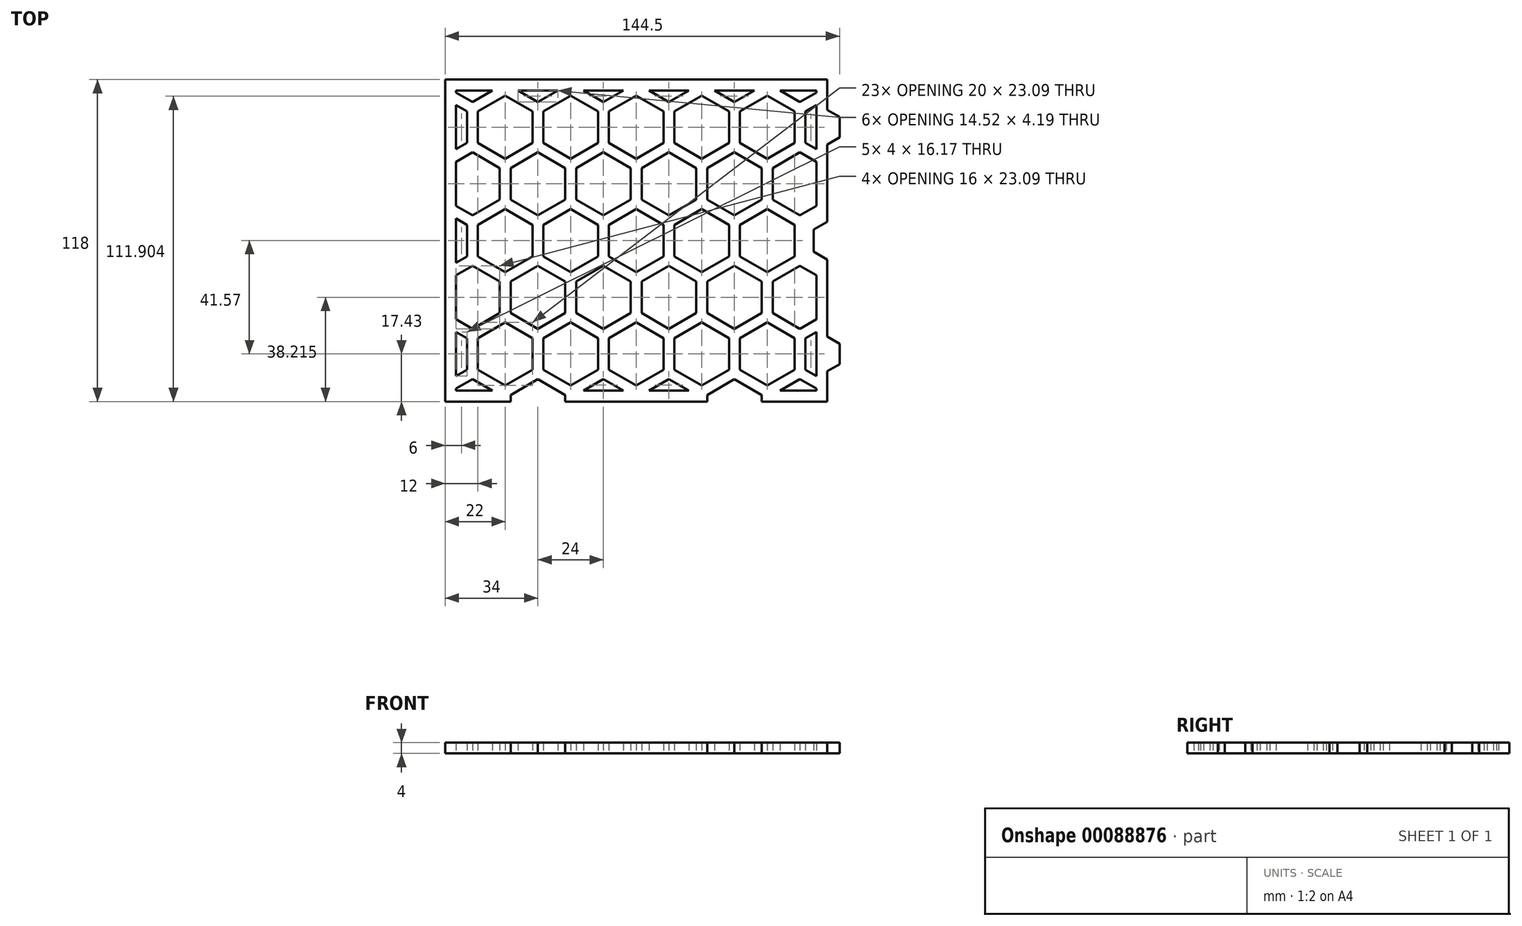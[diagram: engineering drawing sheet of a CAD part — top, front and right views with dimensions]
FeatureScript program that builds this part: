
annotation { "Feature Type Name" : "Feature", "Feature Type Description" : "" }
export const myFeature = defineFeature(function(context is Context, id is Id, definition is map)
    precondition{}
    {
        {
            var Q0;
            Q0=qCreatedBy(makeId("Top.planeOp"),FACE);
            var sketch = newSketch(context, id + "F0", { "sketchPlane" : qUnion([Q0])});
            skLineSegment(sketch, "E0.bottom", {"start": v(70, -59) * mm, "end": v(-70, -59) * mm});
            skLineSegment(sketch, "E0.top", {"start": v(70, 59) * mm, "end": v(-70, 59) * mm});
            skLineSegment(sketch, "E0.left", {"start": v(70, -59) * mm, "end": v(70, 59) * mm});
            skLineSegment(sketch, "E0.right", {"start": v(-70, -59) * mm, "end": v(-70, 59) * mm});
            skPoint(sketch, "E0.middle", {"position": v(0, 0) * mm});
            skLineSegment(sketch, "E1.0", {"start": v(-66, -55) * mm, "end": v(-66, 55) * mm});
            skLineSegment(sketch, "E1.1", {"start": v(66, -55) * mm, "end": v(-66, -55) * mm});
            skLineSegment(sketch, "E1.2", {"start": v(66, -55) * mm, "end": v(66, 55) * mm});
            skLineSegment(sketch, "E1.3", {"start": v(66, 55) * mm, "end": v(-66, 55) * mm});
            skSolve(sketch);
        }
        {
            var Q0;
            Q0=qSketchRegion(id+"F0",true);
            extrude(context, id + "F1", {"entities" : qUnion([Q0]), "depth" : 4 * mm});
        }
        {
            var Q0;
            Q0=qCreatedBy(makeId("Top.planeOp"),FACE);
            var sketch = newSketch(context, id + "F2", { "sketchPlane" : qUnion([Q0])});
            skLineSegment(sketch, "E2.0.1.1", {"start": v(-62, -47.34) * mm, "end": v(-66, -49.65) * mm});
            skLineSegment(sketch, "E2.0.1.5", {"start": v(-66, -33.49) * mm, "end": v(-62, -35.8) * mm});
            skLineSegment(sketch, "E2.0.1.13", {"start": v(-62, -35.8) * mm, "end": v(-62, -47.34) * mm});
            skLineSegment(sketch, "E2.0.2.1", {"start": v(-62, -5.77) * mm, "end": v(-66, -8.08) * mm});
            skLineSegment(sketch, "E2.0.2.5", {"start": v(-66, 8.08) * mm, "end": v(-62, 5.77) * mm});
            skLineSegment(sketch, "E2.0.2.13", {"start": v(-62, 5.77) * mm, "end": v(-62, -5.77) * mm});
            skLineSegment(sketch, "E2.0.3.1", {"start": v(-62, 35.8) * mm, "end": v(-66, 33.49) * mm});
            skLineSegment(sketch, "E2.0.3.5", {"start": v(-66, 49.65) * mm, "end": v(-62, 47.34) * mm});
            skLineSegment(sketch, "E2.0.3.13", {"start": v(-62, 47.34) * mm, "end": v(-62, 35.8) * mm});
            skLineSegment(sketch, "E2.1.0.7", {"start": v(-60, -50.8) * mm, "end": v(-52.74, -55) * mm});
            skLineSegment(sketch, "E2.1.0.8", {"start": v(-66, -54.27) * mm, "end": v(-60, -50.8) * mm});
            skCircle(sketch, "E2.1.1.0", {"center": v(-48, -41.57) * mm, "radius": 11.55 * mm, "construction": true});
            skLineSegment(sketch, "E2.1.1.1", {"start": v(-38, -47.34) * mm, "end": v(-48, -53.12) * mm});
            skLineSegment(sketch, "E2.1.1.2", {"start": v(-48, -53.12) * mm, "end": v(-58, -47.34) * mm});
            skLineSegment(sketch, "E2.1.1.3", {"start": v(-58, -47.34) * mm, "end": v(-58, -35.8) * mm});
            skLineSegment(sketch, "E2.1.1.4", {"start": v(-58, -35.8) * mm, "end": v(-48, -30.02) * mm});
            skLineSegment(sketch, "E2.1.1.5", {"start": v(-48, -30.02) * mm, "end": v(-38, -35.8) * mm});
            skLineSegment(sketch, "E2.1.1.6", {"start": v(-50, -15.01) * mm, "end": v(-50, -26.56) * mm});
            skLineSegment(sketch, "E2.1.1.7", {"start": v(-60, -9.24) * mm, "end": v(-50, -15.01) * mm});
            skLineSegment(sketch, "E2.1.1.8", {"start": v(-66, -12.7) * mm, "end": v(-60, -9.24) * mm});
            skLineSegment(sketch, "E2.1.1.10", {"start": v(-60, -32.33) * mm, "end": v(-66, -28.87) * mm});
            skLineSegment(sketch, "E2.1.1.11", {"start": v(-50, -26.56) * mm, "end": v(-60, -32.33) * mm});
            skLineSegment(sketch, "E2.1.1.13", {"start": v(-38, -35.8) * mm, "end": v(-38, -47.34) * mm});
            skCircle(sketch, "E2.1.2.0", {"center": v(-48, 0) * mm, "radius": 11.55 * mm, "construction": true});
            skLineSegment(sketch, "E2.1.2.1", {"start": v(-38, -5.77) * mm, "end": v(-48, -11.55) * mm});
            skLineSegment(sketch, "E2.1.2.2", {"start": v(-48, -11.55) * mm, "end": v(-58, -5.77) * mm});
            skLineSegment(sketch, "E2.1.2.3", {"start": v(-58, -5.77) * mm, "end": v(-58, 5.77) * mm});
            skLineSegment(sketch, "E2.1.2.4", {"start": v(-58, 5.77) * mm, "end": v(-48, 11.55) * mm});
            skLineSegment(sketch, "E2.1.2.5", {"start": v(-48, 11.55) * mm, "end": v(-38, 5.77) * mm});
            skLineSegment(sketch, "E2.1.2.6", {"start": v(-50, 26.56) * mm, "end": v(-50, 15.01) * mm});
            skLineSegment(sketch, "E2.1.2.7", {"start": v(-60, 32.33) * mm, "end": v(-50, 26.56) * mm});
            skLineSegment(sketch, "E2.1.2.8", {"start": v(-66, 28.87) * mm, "end": v(-60, 32.33) * mm});
            skLineSegment(sketch, "E2.1.2.10", {"start": v(-60, 9.24) * mm, "end": v(-66, 12.7) * mm});
            skLineSegment(sketch, "E2.1.2.11", {"start": v(-50, 15.01) * mm, "end": v(-60, 9.24) * mm});
            skLineSegment(sketch, "E2.1.2.13", {"start": v(-38, 5.77) * mm, "end": v(-38, -5.77) * mm});
            skCircle(sketch, "E2.1.3.0", {"center": v(-48, 41.57) * mm, "radius": 11.55 * mm, "construction": true});
            skLineSegment(sketch, "E2.1.3.1", {"start": v(-38, 35.8) * mm, "end": v(-48, 30.02) * mm});
            skLineSegment(sketch, "E2.1.3.2", {"start": v(-48, 30.02) * mm, "end": v(-58, 35.8) * mm});
            skLineSegment(sketch, "E2.1.3.3", {"start": v(-58, 35.8) * mm, "end": v(-58, 47.34) * mm});
            skLineSegment(sketch, "E2.1.3.4", {"start": v(-58, 47.34) * mm, "end": v(-48, 53.12) * mm});
            skLineSegment(sketch, "E2.1.3.5", {"start": v(-48, 53.12) * mm, "end": v(-38, 47.34) * mm});
            skLineSegment(sketch, "E2.1.3.10", {"start": v(-60, 50.8) * mm, "end": v(-66, 54.27) * mm});
            skLineSegment(sketch, "E2.1.3.11", {"start": v(-52.74, 55) * mm, "end": v(-60, 50.8) * mm});
            skLineSegment(sketch, "E2.1.3.13", {"start": v(-38, 47.34) * mm, "end": v(-38, 35.8) * mm});
            skLineSegment(sketch, "E2.2.0.7", {"start": v(-36, -50.8) * mm, "end": v(-28.74, -55) * mm});
            skLineSegment(sketch, "E2.2.0.8", {"start": v(-43.26, -55) * mm, "end": v(-36, -50.8) * mm});
            skCircle(sketch, "E2.2.1.0", {"center": v(-24, -41.57) * mm, "radius": 11.55 * mm, "construction": true});
            skLineSegment(sketch, "E2.2.1.1", {"start": v(-14, -47.34) * mm, "end": v(-24, -53.12) * mm});
            skLineSegment(sketch, "E2.2.1.2", {"start": v(-24, -53.12) * mm, "end": v(-34, -47.34) * mm});
            skLineSegment(sketch, "E2.2.1.3", {"start": v(-34, -47.34) * mm, "end": v(-34, -35.8) * mm});
            skLineSegment(sketch, "E2.2.1.4", {"start": v(-34, -35.8) * mm, "end": v(-24, -30.02) * mm});
            skLineSegment(sketch, "E2.2.1.5", {"start": v(-24, -30.02) * mm, "end": v(-14, -35.8) * mm});
            skLineSegment(sketch, "E2.2.1.6", {"start": v(-26, -15.01) * mm, "end": v(-26, -26.56) * mm});
            skLineSegment(sketch, "E2.2.1.7", {"start": v(-36, -9.24) * mm, "end": v(-26, -15.01) * mm});
            skLineSegment(sketch, "E2.2.1.8", {"start": v(-46, -15.01) * mm, "end": v(-36, -9.24) * mm});
            skLineSegment(sketch, "E2.2.1.9", {"start": v(-46, -26.56) * mm, "end": v(-46, -15.01) * mm});
            skLineSegment(sketch, "E2.2.1.10", {"start": v(-36, -32.33) * mm, "end": v(-46, -26.56) * mm});
            skLineSegment(sketch, "E2.2.1.11", {"start": v(-26, -26.56) * mm, "end": v(-36, -32.33) * mm});
            skCircle(sketch, "E2.2.1.12", {"center": v(-36, -20.79) * mm, "radius": 11.55 * mm, "construction": true});
            skLineSegment(sketch, "E2.2.1.13", {"start": v(-14, -35.8) * mm, "end": v(-14, -47.34) * mm});
            skCircle(sketch, "E2.2.2.0", {"center": v(-24, 0) * mm, "radius": 11.55 * mm, "construction": true});
            skLineSegment(sketch, "E2.2.2.1", {"start": v(-14, -5.77) * mm, "end": v(-24, -11.55) * mm});
            skLineSegment(sketch, "E2.2.2.2", {"start": v(-24, -11.55) * mm, "end": v(-34, -5.77) * mm});
            skLineSegment(sketch, "E2.2.2.3", {"start": v(-34, -5.77) * mm, "end": v(-34, 5.77) * mm});
            skLineSegment(sketch, "E2.2.2.4", {"start": v(-34, 5.77) * mm, "end": v(-24, 11.55) * mm});
            skLineSegment(sketch, "E2.2.2.5", {"start": v(-24, 11.55) * mm, "end": v(-14, 5.77) * mm});
            skLineSegment(sketch, "E2.2.2.6", {"start": v(-26, 26.56) * mm, "end": v(-26, 15.01) * mm});
            skLineSegment(sketch, "E2.2.2.7", {"start": v(-36, 32.33) * mm, "end": v(-26, 26.56) * mm});
            skLineSegment(sketch, "E2.2.2.8", {"start": v(-46, 26.56) * mm, "end": v(-36, 32.33) * mm});
            skLineSegment(sketch, "E2.2.2.9", {"start": v(-46, 15.01) * mm, "end": v(-46, 26.56) * mm});
            skLineSegment(sketch, "E2.2.2.10", {"start": v(-36, 9.24) * mm, "end": v(-46, 15.01) * mm});
            skLineSegment(sketch, "E2.2.2.11", {"start": v(-26, 15.01) * mm, "end": v(-36, 9.24) * mm});
            skCircle(sketch, "E2.2.2.12", {"center": v(-36, 20.78) * mm, "radius": 11.55 * mm, "construction": true});
            skLineSegment(sketch, "E2.2.2.13", {"start": v(-14, 5.77) * mm, "end": v(-14, -5.77) * mm});
            skCircle(sketch, "E2.2.3.0", {"center": v(-24, 41.57) * mm, "radius": 11.55 * mm, "construction": true});
            skLineSegment(sketch, "E2.2.3.1", {"start": v(-14, 35.8) * mm, "end": v(-24, 30.02) * mm});
            skLineSegment(sketch, "E2.2.3.2", {"start": v(-24, 30.02) * mm, "end": v(-34, 35.8) * mm});
            skLineSegment(sketch, "E2.2.3.3", {"start": v(-34, 35.8) * mm, "end": v(-34, 47.34) * mm});
            skLineSegment(sketch, "E2.2.3.4", {"start": v(-34, 47.34) * mm, "end": v(-24, 53.12) * mm});
            skLineSegment(sketch, "E2.2.3.5", {"start": v(-24, 53.12) * mm, "end": v(-14, 47.34) * mm});
            skLineSegment(sketch, "E2.2.3.10", {"start": v(-36, 50.8) * mm, "end": v(-43.26, 55) * mm});
            skLineSegment(sketch, "E2.2.3.11", {"start": v(-28.74, 55) * mm, "end": v(-36, 50.8) * mm});
            skLineSegment(sketch, "E2.2.3.13", {"start": v(-14, 47.34) * mm, "end": v(-14, 35.8) * mm});
            skLineSegment(sketch, "E2.3.0.7", {"start": v(-12, -50.8) * mm, "end": v(-4.74, -55) * mm});
            skLineSegment(sketch, "E2.3.0.8", {"start": v(-19.26, -55) * mm, "end": v(-12, -50.8) * mm});
            skCircle(sketch, "E2.3.1.0", {"center": v(0, -41.57) * mm, "radius": 11.55 * mm, "construction": true});
            skLineSegment(sketch, "E2.3.1.1", {"start": v(10, -47.34) * mm, "end": v(0, -53.12) * mm});
            skLineSegment(sketch, "E2.3.1.2", {"start": v(0, -53.12) * mm, "end": v(-10, -47.34) * mm});
            skLineSegment(sketch, "E2.3.1.3", {"start": v(-10, -47.34) * mm, "end": v(-10, -35.8) * mm});
            skLineSegment(sketch, "E2.3.1.4", {"start": v(-10, -35.8) * mm, "end": v(0, -30.02) * mm});
            skLineSegment(sketch, "E2.3.1.5", {"start": v(0, -30.02) * mm, "end": v(10, -35.8) * mm});
            skLineSegment(sketch, "E2.3.1.6", {"start": v(-2, -15.01) * mm, "end": v(-2, -26.56) * mm});
            skLineSegment(sketch, "E2.3.1.7", {"start": v(-12, -9.24) * mm, "end": v(-2, -15.01) * mm});
            skLineSegment(sketch, "E2.3.1.8", {"start": v(-22, -15.01) * mm, "end": v(-12, -9.24) * mm});
            skLineSegment(sketch, "E2.3.1.9", {"start": v(-22, -26.56) * mm, "end": v(-22, -15.01) * mm});
            skLineSegment(sketch, "E2.3.1.10", {"start": v(-12, -32.33) * mm, "end": v(-22, -26.56) * mm});
            skLineSegment(sketch, "E2.3.1.11", {"start": v(-2, -26.56) * mm, "end": v(-12, -32.33) * mm});
            skCircle(sketch, "E2.3.1.12", {"center": v(-12, -20.79) * mm, "radius": 11.55 * mm, "construction": true});
            skLineSegment(sketch, "E2.3.1.13", {"start": v(10, -35.8) * mm, "end": v(10, -47.34) * mm});
            skCircle(sketch, "E2.3.2.0", {"center": v(0, 0) * mm, "radius": 11.55 * mm, "construction": true});
            skLineSegment(sketch, "E2.3.2.1", {"start": v(10, -5.77) * mm, "end": v(0, -11.55) * mm});
            skLineSegment(sketch, "E2.3.2.2", {"start": v(0, -11.55) * mm, "end": v(-10, -5.77) * mm});
            skLineSegment(sketch, "E2.3.2.3", {"start": v(-10, -5.77) * mm, "end": v(-10, 5.77) * mm});
            skLineSegment(sketch, "E2.3.2.4", {"start": v(-10, 5.77) * mm, "end": v(0, 11.55) * mm});
            skLineSegment(sketch, "E2.3.2.5", {"start": v(0, 11.55) * mm, "end": v(10, 5.77) * mm});
            skLineSegment(sketch, "E2.3.2.6", {"start": v(-2, 26.56) * mm, "end": v(-2, 15.01) * mm});
            skLineSegment(sketch, "E2.3.2.7", {"start": v(-12, 32.33) * mm, "end": v(-2, 26.56) * mm});
            skLineSegment(sketch, "E2.3.2.8", {"start": v(-22, 26.56) * mm, "end": v(-12, 32.33) * mm});
            skLineSegment(sketch, "E2.3.2.9", {"start": v(-22, 15.01) * mm, "end": v(-22, 26.56) * mm});
            skLineSegment(sketch, "E2.3.2.10", {"start": v(-12, 9.24) * mm, "end": v(-22, 15.01) * mm});
            skLineSegment(sketch, "E2.3.2.11", {"start": v(-2, 15.01) * mm, "end": v(-12, 9.24) * mm});
            skCircle(sketch, "E2.3.2.12", {"center": v(-12, 20.78) * mm, "radius": 11.55 * mm, "construction": true});
            skLineSegment(sketch, "E2.3.2.13", {"start": v(10, 5.77) * mm, "end": v(10, -5.77) * mm});
            skCircle(sketch, "E2.3.3.0", {"center": v(0, 41.57) * mm, "radius": 11.55 * mm, "construction": true});
            skLineSegment(sketch, "E2.3.3.1", {"start": v(10, 35.8) * mm, "end": v(0, 30.02) * mm});
            skLineSegment(sketch, "E2.3.3.2", {"start": v(0, 30.02) * mm, "end": v(-10, 35.8) * mm});
            skLineSegment(sketch, "E2.3.3.3", {"start": v(-10, 35.8) * mm, "end": v(-10, 47.34) * mm});
            skLineSegment(sketch, "E2.3.3.4", {"start": v(-10, 47.34) * mm, "end": v(0, 53.12) * mm});
            skLineSegment(sketch, "E2.3.3.5", {"start": v(0, 53.12) * mm, "end": v(10, 47.34) * mm});
            skLineSegment(sketch, "E2.3.3.10", {"start": v(-12, 50.8) * mm, "end": v(-19.26, 55) * mm});
            skLineSegment(sketch, "E2.3.3.11", {"start": v(-4.74, 55) * mm, "end": v(-12, 50.8) * mm});
            skLineSegment(sketch, "E2.3.3.13", {"start": v(10, 47.34) * mm, "end": v(10, 35.8) * mm});
            skLineSegment(sketch, "E2.4.0.7", {"start": v(12, -50.8) * mm, "end": v(19.26, -55) * mm});
            skLineSegment(sketch, "E2.4.0.8", {"start": v(4.74, -55) * mm, "end": v(12, -50.8) * mm});
            skCircle(sketch, "E2.4.1.0", {"center": v(24, -41.57) * mm, "radius": 11.55 * mm, "construction": true});
            skLineSegment(sketch, "E2.4.1.1", {"start": v(34, -47.34) * mm, "end": v(24, -53.12) * mm});
            skLineSegment(sketch, "E2.4.1.2", {"start": v(24, -53.12) * mm, "end": v(14, -47.34) * mm});
            skLineSegment(sketch, "E2.4.1.3", {"start": v(14, -47.34) * mm, "end": v(14, -35.8) * mm});
            skLineSegment(sketch, "E2.4.1.4", {"start": v(14, -35.8) * mm, "end": v(24, -30.02) * mm});
            skLineSegment(sketch, "E2.4.1.5", {"start": v(24, -30.02) * mm, "end": v(34, -35.8) * mm});
            skLineSegment(sketch, "E2.4.1.6", {"start": v(22, -15.01) * mm, "end": v(22, -26.56) * mm});
            skLineSegment(sketch, "E2.4.1.7", {"start": v(12, -9.24) * mm, "end": v(22, -15.01) * mm});
            skLineSegment(sketch, "E2.4.1.8", {"start": v(2, -15.01) * mm, "end": v(12, -9.24) * mm});
            skLineSegment(sketch, "E2.4.1.9", {"start": v(2, -26.56) * mm, "end": v(2, -15.01) * mm});
            skLineSegment(sketch, "E2.4.1.10", {"start": v(12, -32.33) * mm, "end": v(2, -26.56) * mm});
            skLineSegment(sketch, "E2.4.1.11", {"start": v(22, -26.56) * mm, "end": v(12, -32.33) * mm});
            skCircle(sketch, "E2.4.1.12", {"center": v(12, -20.79) * mm, "radius": 11.55 * mm, "construction": true});
            skLineSegment(sketch, "E2.4.1.13", {"start": v(34, -35.8) * mm, "end": v(34, -47.34) * mm});
            skCircle(sketch, "E2.4.2.0", {"center": v(24, 0) * mm, "radius": 11.55 * mm, "construction": true});
            skLineSegment(sketch, "E2.4.2.1", {"start": v(34, -5.77) * mm, "end": v(24, -11.55) * mm});
            skLineSegment(sketch, "E2.4.2.2", {"start": v(24, -11.55) * mm, "end": v(14, -5.77) * mm});
            skLineSegment(sketch, "E2.4.2.3", {"start": v(14, -5.77) * mm, "end": v(14, 5.77) * mm});
            skLineSegment(sketch, "E2.4.2.4", {"start": v(14, 5.77) * mm, "end": v(24, 11.55) * mm});
            skLineSegment(sketch, "E2.4.2.5", {"start": v(24, 11.55) * mm, "end": v(34, 5.77) * mm});
            skLineSegment(sketch, "E2.4.2.6", {"start": v(22, 26.56) * mm, "end": v(22, 15.01) * mm});
            skLineSegment(sketch, "E2.4.2.7", {"start": v(12, 32.33) * mm, "end": v(22, 26.56) * mm});
            skLineSegment(sketch, "E2.4.2.8", {"start": v(2, 26.56) * mm, "end": v(12, 32.33) * mm});
            skLineSegment(sketch, "E2.4.2.9", {"start": v(2, 15.01) * mm, "end": v(2, 26.56) * mm});
            skLineSegment(sketch, "E2.4.2.10", {"start": v(12, 9.24) * mm, "end": v(2, 15.01) * mm});
            skLineSegment(sketch, "E2.4.2.11", {"start": v(22, 15.01) * mm, "end": v(12, 9.24) * mm});
            skCircle(sketch, "E2.4.2.12", {"center": v(12, 20.78) * mm, "radius": 11.55 * mm, "construction": true});
            skLineSegment(sketch, "E2.4.2.13", {"start": v(34, 5.77) * mm, "end": v(34, -5.77) * mm});
            skCircle(sketch, "E2.4.3.0", {"center": v(24, 41.57) * mm, "radius": 11.55 * mm, "construction": true});
            skLineSegment(sketch, "E2.4.3.1", {"start": v(34, 35.8) * mm, "end": v(24, 30.02) * mm});
            skLineSegment(sketch, "E2.4.3.2", {"start": v(24, 30.02) * mm, "end": v(14, 35.8) * mm});
            skLineSegment(sketch, "E2.4.3.3", {"start": v(14, 35.8) * mm, "end": v(14, 47.34) * mm});
            skLineSegment(sketch, "E2.4.3.4", {"start": v(14, 47.34) * mm, "end": v(24, 53.12) * mm});
            skLineSegment(sketch, "E2.4.3.5", {"start": v(24, 53.12) * mm, "end": v(34, 47.34) * mm});
            skLineSegment(sketch, "E2.4.3.10", {"start": v(12, 50.8) * mm, "end": v(4.74, 55) * mm});
            skLineSegment(sketch, "E2.4.3.11", {"start": v(19.26, 55) * mm, "end": v(12, 50.8) * mm});
            skLineSegment(sketch, "E2.4.3.13", {"start": v(34, 47.34) * mm, "end": v(34, 35.8) * mm});
            skLineSegment(sketch, "E2.5.0.7", {"start": v(36, -50.8) * mm, "end": v(43.26, -55) * mm});
            skLineSegment(sketch, "E2.5.0.8", {"start": v(28.74, -55) * mm, "end": v(36, -50.8) * mm});
            skCircle(sketch, "E2.5.1.0", {"center": v(48, -41.57) * mm, "radius": 11.55 * mm, "construction": true});
            skLineSegment(sketch, "E2.5.1.1", {"start": v(58, -47.34) * mm, "end": v(48, -53.12) * mm});
            skLineSegment(sketch, "E2.5.1.2", {"start": v(48, -53.12) * mm, "end": v(38, -47.34) * mm});
            skLineSegment(sketch, "E2.5.1.3", {"start": v(38, -47.34) * mm, "end": v(38, -35.8) * mm});
            skLineSegment(sketch, "E2.5.1.4", {"start": v(38, -35.8) * mm, "end": v(48, -30.02) * mm});
            skLineSegment(sketch, "E2.5.1.5", {"start": v(48, -30.02) * mm, "end": v(58, -35.8) * mm});
            skLineSegment(sketch, "E2.5.1.6", {"start": v(46, -15.01) * mm, "end": v(46, -26.56) * mm});
            skLineSegment(sketch, "E2.5.1.7", {"start": v(36, -9.24) * mm, "end": v(46, -15.01) * mm});
            skLineSegment(sketch, "E2.5.1.8", {"start": v(26, -15.01) * mm, "end": v(36, -9.24) * mm});
            skLineSegment(sketch, "E2.5.1.9", {"start": v(26, -26.56) * mm, "end": v(26, -15.01) * mm});
            skLineSegment(sketch, "E2.5.1.10", {"start": v(36, -32.33) * mm, "end": v(26, -26.56) * mm});
            skLineSegment(sketch, "E2.5.1.11", {"start": v(46, -26.56) * mm, "end": v(36, -32.33) * mm});
            skCircle(sketch, "E2.5.1.12", {"center": v(36, -20.79) * mm, "radius": 11.55 * mm, "construction": true});
            skLineSegment(sketch, "E2.5.1.13", {"start": v(58, -35.8) * mm, "end": v(58, -47.34) * mm});
            skCircle(sketch, "E2.5.2.0", {"center": v(48, 0) * mm, "radius": 11.55 * mm, "construction": true});
            skLineSegment(sketch, "E2.5.2.1", {"start": v(58, -5.77) * mm, "end": v(48, -11.55) * mm});
            skLineSegment(sketch, "E2.5.2.2", {"start": v(48, -11.55) * mm, "end": v(38, -5.77) * mm});
            skLineSegment(sketch, "E2.5.2.3", {"start": v(38, -5.77) * mm, "end": v(38, 5.77) * mm});
            skLineSegment(sketch, "E2.5.2.4", {"start": v(38, 5.77) * mm, "end": v(48, 11.55) * mm});
            skLineSegment(sketch, "E2.5.2.5", {"start": v(48, 11.55) * mm, "end": v(58, 5.77) * mm});
            skLineSegment(sketch, "E2.5.2.6", {"start": v(46, 26.56) * mm, "end": v(46, 15.01) * mm});
            skLineSegment(sketch, "E2.5.2.7", {"start": v(36, 32.33) * mm, "end": v(46, 26.56) * mm});
            skLineSegment(sketch, "E2.5.2.8", {"start": v(26, 26.56) * mm, "end": v(36, 32.33) * mm});
            skLineSegment(sketch, "E2.5.2.9", {"start": v(26, 15.01) * mm, "end": v(26, 26.56) * mm});
            skLineSegment(sketch, "E2.5.2.10", {"start": v(36, 9.24) * mm, "end": v(26, 15.01) * mm});
            skLineSegment(sketch, "E2.5.2.11", {"start": v(46, 15.01) * mm, "end": v(36, 9.24) * mm});
            skCircle(sketch, "E2.5.2.12", {"center": v(36, 20.78) * mm, "radius": 11.55 * mm, "construction": true});
            skLineSegment(sketch, "E2.5.2.13", {"start": v(58, 5.77) * mm, "end": v(58, -5.77) * mm});
            skCircle(sketch, "E2.5.3.0", {"center": v(48, 41.57) * mm, "radius": 11.55 * mm, "construction": true});
            skLineSegment(sketch, "E2.5.3.1", {"start": v(58, 35.8) * mm, "end": v(48, 30.02) * mm});
            skLineSegment(sketch, "E2.5.3.2", {"start": v(48, 30.02) * mm, "end": v(38, 35.8) * mm});
            skLineSegment(sketch, "E2.5.3.3", {"start": v(38, 35.8) * mm, "end": v(38, 47.34) * mm});
            skLineSegment(sketch, "E2.5.3.4", {"start": v(38, 47.34) * mm, "end": v(48, 53.12) * mm});
            skLineSegment(sketch, "E2.5.3.5", {"start": v(48, 53.12) * mm, "end": v(58, 47.34) * mm});
            skLineSegment(sketch, "E2.5.3.10", {"start": v(36, 50.8) * mm, "end": v(28.74, 55) * mm});
            skLineSegment(sketch, "E2.5.3.11", {"start": v(43.26, 55) * mm, "end": v(36, 50.8) * mm});
            skLineSegment(sketch, "E2.5.3.13", {"start": v(58, 47.34) * mm, "end": v(58, 35.8) * mm});
            skLineSegment(sketch, "E2.6.0.7", {"start": v(60, -50.8) * mm, "end": v(66, -54.27) * mm});
            skLineSegment(sketch, "E2.6.0.8", {"start": v(52.74, -55) * mm, "end": v(60, -50.8) * mm});
            skLineSegment(sketch, "E2.6.1.2", {"start": v(66, -49.65) * mm, "end": v(62, -47.34) * mm});
            skLineSegment(sketch, "E2.6.1.3", {"start": v(62, -47.34) * mm, "end": v(62, -35.8) * mm});
            skLineSegment(sketch, "E2.6.1.4", {"start": v(62, -35.8) * mm, "end": v(66, -33.49) * mm});
            skLineSegment(sketch, "E2.6.1.7", {"start": v(60, -9.24) * mm, "end": v(66, -12.7) * mm});
            skLineSegment(sketch, "E2.6.1.8", {"start": v(50, -15.01) * mm, "end": v(60, -9.24) * mm});
            skLineSegment(sketch, "E2.6.1.9", {"start": v(50, -26.56) * mm, "end": v(50, -15.01) * mm});
            skLineSegment(sketch, "E2.6.1.10", {"start": v(60, -32.33) * mm, "end": v(50, -26.56) * mm});
            skLineSegment(sketch, "E2.6.1.11", {"start": v(66, -28.87) * mm, "end": v(60, -32.33) * mm});
            skLineSegment(sketch, "E2.6.2.2", {"start": v(66, -8.08) * mm, "end": v(62, -5.77) * mm});
            skLineSegment(sketch, "E2.6.2.3", {"start": v(62, -5.77) * mm, "end": v(62, 5.77) * mm});
            skLineSegment(sketch, "E2.6.2.4", {"start": v(62, 5.77) * mm, "end": v(66, 8.08) * mm});
            skLineSegment(sketch, "E2.6.2.7", {"start": v(60, 32.33) * mm, "end": v(66, 28.87) * mm});
            skLineSegment(sketch, "E2.6.2.8", {"start": v(50, 26.56) * mm, "end": v(60, 32.33) * mm});
            skLineSegment(sketch, "E2.6.2.9", {"start": v(50, 15.01) * mm, "end": v(50, 26.56) * mm});
            skLineSegment(sketch, "E2.6.2.10", {"start": v(60, 9.24) * mm, "end": v(50, 15.01) * mm});
            skLineSegment(sketch, "E2.6.2.11", {"start": v(66, 12.7) * mm, "end": v(60, 9.24) * mm});
            skLineSegment(sketch, "E2.6.3.2", {"start": v(66, 33.49) * mm, "end": v(62, 35.8) * mm});
            skLineSegment(sketch, "E2.6.3.3", {"start": v(62, 35.8) * mm, "end": v(62, 47.34) * mm});
            skLineSegment(sketch, "E2.6.3.4", {"start": v(62, 47.34) * mm, "end": v(66, 49.65) * mm});
            skLineSegment(sketch, "E2.6.3.10", {"start": v(60, 50.8) * mm, "end": v(52.74, 55) * mm});
            skLineSegment(sketch, "E2.6.3.11", {"start": v(66, 54.27) * mm, "end": v(60, 50.8) * mm});
            skLineSegment(sketch, "E3.0", {"start": v(-66, -55) * mm, "end": v(-66, -54.27) * mm});
            skLineSegment(sketch, "E3.1", {"start": v(66, 55) * mm, "end": v(52.74, 55) * mm});
            skLineSegment(sketch, "E3.2", {"start": v(66, -55) * mm, "end": v(66, -54.27) * mm});
            skLineSegment(sketch, "E3.3", {"start": v(66, -55) * mm, "end": v(52.74, -55) * mm});
            skLineSegment(sketch, "E4.trimOffspring", {"start": v(-66, 54.27) * mm, "end": v(-66, 55) * mm});
            skLineSegment(sketch, "E5.trimOffspring", {"start": v(-66, 33.49) * mm, "end": v(-66, 49.65) * mm});
            skLineSegment(sketch, "E6.trimOffspring", {"start": v(-66, 12.7) * mm, "end": v(-66, 28.87) * mm});
            skLineSegment(sketch, "E7.trimOffspring", {"start": v(-52.74, 55) * mm, "end": v(-66, 55) * mm});
            skLineSegment(sketch, "E8.trimOffspring", {"start": v(-28.74, 55) * mm, "end": v(-43.26, 55) * mm});
            skLineSegment(sketch, "E9.trimOffspring", {"start": v(-4.74, 55) * mm, "end": v(-19.26, 55) * mm});
            skLineSegment(sketch, "E10.trimOffspring", {"start": v(19.26, 55) * mm, "end": v(4.74, 55) * mm});
            skLineSegment(sketch, "E11.trimOffspring", {"start": v(43.26, 55) * mm, "end": v(28.74, 55) * mm});
            skLineSegment(sketch, "E12.trimOffspring", {"start": v(66, 54.27) * mm, "end": v(66, 55) * mm});
            skLineSegment(sketch, "E13.trimOffspring", {"start": v(66, 33.49) * mm, "end": v(66, 49.65) * mm});
            skLineSegment(sketch, "E14.trimOffspring", {"start": v(66, 12.7) * mm, "end": v(66, 28.87) * mm});
            skLineSegment(sketch, "E15.trimOffspring", {"start": v(66, -8.08) * mm, "end": v(66, 8.08) * mm});
            skLineSegment(sketch, "E16.trimOffspring", {"start": v(66, -28.87) * mm, "end": v(66, -12.7) * mm});
            skLineSegment(sketch, "E17.trimOffspring", {"start": v(66, -49.65) * mm, "end": v(66, -33.49) * mm});
            skLineSegment(sketch, "E18.trimOffspring", {"start": v(43.26, -55) * mm, "end": v(28.74, -55) * mm});
            skLineSegment(sketch, "E19.trimOffspring", {"start": v(19.26, -55) * mm, "end": v(4.74, -55) * mm});
            skLineSegment(sketch, "E20.trimOffspring", {"start": v(-4.74, -55) * mm, "end": v(-19.26, -55) * mm});
            skLineSegment(sketch, "E21.trimOffspring", {"start": v(-28.74, -55) * mm, "end": v(-43.26, -55) * mm});
            skLineSegment(sketch, "E22.trimOffspring", {"start": v(-52.74, -55) * mm, "end": v(-66, -55) * mm});
            skLineSegment(sketch, "E23.trimOffspring", {"start": v(-66, -49.65) * mm, "end": v(-66, -33.49) * mm});
            skLineSegment(sketch, "E24.trimOffspring", {"start": v(-66, -28.87) * mm, "end": v(-66, -12.7) * mm});
            skLineSegment(sketch, "E25.trimOffspring", {"start": v(-66, -8.08) * mm, "end": v(-66, 8.08) * mm});
            skLineSegment(sketch, "E26.0", {"start": v(-70, -59) * mm, "end": v(-70, 59) * mm});
            skLineSegment(sketch, "E26.1", {"start": v(70, 59) * mm, "end": v(-70, 59) * mm});
            skLineSegment(sketch, "E26.2", {"start": v(70, -59) * mm, "end": v(70, 59) * mm});
            skLineSegment(sketch, "E26.3", {"start": v(70, -59) * mm, "end": v(-70, -59) * mm});
            skSolve(sketch);
        }
        {
            var Q0;
            Q0=qSketchRegion(id+"F2",true);
            var Q1;
            Q1=makeQuery(id+"F1.opExtrude","CAP_FACE",FACE,{"disambiguationData":[OSD([sQuery(id+"F0.wireOp",EDGE,"E0.bottom"),sQuery(id+"F0.wireOp",EDGE,"E0.top"),sQuery(id+"F0.wireOp",EDGE,"E0.left"),sQuery(id+"F0.wireOp",EDGE,"E0.right"),sQuery(id+"F0.wireOp",EDGE,"E1.0"),sQuery(id+"F0.wireOp",EDGE,"E1.1"),sQuery(id+"F0.wireOp",EDGE,"E1.2"),sQuery(id+"F0.wireOp",EDGE,"E1.3")])],"isStart":false});
            extrude(context, id + "F3", {"entities" : qUnion([Q0]), "operationType" : NewBodyOperationType.ADD, "endBound" : BoundingType.UP_TO_SURFACE, "endBoundEntityFace" : qUnion([Q1]), "depth" : 4 * mm});
        }
        {
            var Q0;
            Q0=qCreatedBy(makeId("Top.planeOp"),FACE);
            var sketch = newSketch(context, id + "F4", { "sketchPlane" : qUnion([Q0])});
            skCircle(sketch, "E27.cCircle", {"center": v(68, 41.57) * mm, "radius": 11.55 * mm, "construction": true});
            skLineSegment(sketch, "E27.0", {"start": v(78, 35.8) * mm, "end": v(70, 31.18) * mm, "construction": true});
            skLineSegment(sketch, "E27.4", {"start": v(70, 51.96) * mm, "end": v(78, 47.34) * mm, "construction": true});
            skLineSegment(sketch, "E27.5", {"start": v(78, 47.34) * mm, "end": v(78, 35.8) * mm, "construction": true});
            skCircle(sketch, "E28.cCircle", {"center": v(68, -41.57) * mm, "radius": 11.55 * mm, "construction": true});
            skLineSegment(sketch, "E28.3", {"start": v(70, -31.18) * mm, "end": v(78, -35.8) * mm, "construction": true});
            skLineSegment(sketch, "E28.4", {"start": v(78, -35.8) * mm, "end": v(78, -47.34) * mm, "construction": true});
            skLineSegment(sketch, "E28.5", {"start": v(78, -47.34) * mm, "end": v(70, -51.96) * mm, "construction": true});
            skLineSegment(sketch, "E29.0", {"start": v(70, -59) * mm, "end": v(70, 59) * mm});
            skPoint(sketch, "E30.orphan", {"position": v(68, -30.02) * mm});
            skLineSegment(sketch, "E31.0", {"start": v(74.5, 37.82) * mm, "end": v(68.25, 34.2) * mm});
            skLineSegment(sketch, "E31.1", {"start": v(74.5, 45.32) * mm, "end": v(74.5, 37.82) * mm});
            skLineSegment(sketch, "E31.2", {"start": v(68.25, 48.93) * mm, "end": v(74.5, 45.32) * mm});
            skLineSegment(sketch, "E32.0", {"start": v(74.5, -45.32) * mm, "end": v(68.25, -48.93) * mm});
            skLineSegment(sketch, "E32.1", {"start": v(74.5, -37.82) * mm, "end": v(74.5, -45.32) * mm});
            skLineSegment(sketch, "E32.2", {"start": v(68.25, -34.2) * mm, "end": v(74.5, -37.82) * mm});
            skSolve(sketch);
        }
        {
            var Q0;
            Q0 = qSketchRegion(id + "F4", true);
            var Q1;
            Q1=makeQuery(id+"F3.boolean.opBoolean","MERGE",FACE,{"derivedFrom":[makeQuery(id+"F1.opExtrude","CAP_FACE",FACE,{"disambiguationData":[OSD([sQuery(id+"F0.wireOp",EDGE,"E0.bottom"),sQuery(id+"F0.wireOp",EDGE,"E0.top"),sQuery(id+"F0.wireOp",EDGE,"E0.left"),sQuery(id+"F0.wireOp",EDGE,"E0.right"),sQuery(id+"F0.wireOp",EDGE,"E1.0"),sQuery(id+"F0.wireOp",EDGE,"E1.1"),sQuery(id+"F0.wireOp",EDGE,"E1.2"),sQuery(id+"F0.wireOp",EDGE,"E1.3")])],"isStart":false}),makeQuery(id+"F3.opExtrude","CAP_FACE",FACE,{"disambiguationData":[OSD([sQuery(id+"F2.wireOp",EDGE,"E2.0.1.1"),sQuery(id+"F2.wireOp",EDGE,"E2.0.1.5"),sQuery(id+"F2.wireOp",EDGE,"E2.0.1.13"),sQuery(id+"F2.wireOp",EDGE,"E2.0.2.1"),sQuery(id+"F2.wireOp",EDGE,"E2.0.2.5"),sQuery(id+"F2.wireOp",EDGE,"E2.0.2.13"),sQuery(id+"F2.wireOp",EDGE,"E2.0.3.1"),sQuery(id+"F2.wireOp",EDGE,"E2.0.3.5"),sQuery(id+"F2.wireOp",EDGE,"E2.0.3.13"),sQuery(id+"F2.wireOp",EDGE,"E2.1.0.7"),sQuery(id+"F2.wireOp",EDGE,"E2.1.0.8"),sQuery(id+"F2.wireOp",EDGE,"E2.1.1.1"),sQuery(id+"F2.wireOp",EDGE,"E2.1.1.2"),sQuery(id+"F2.wireOp",EDGE,"E2.1.1.3"),sQuery(id+"F2.wireOp",EDGE,"E2.1.1.4"),sQuery(id+"F2.wireOp",EDGE,"E2.1.1.5"),sQuery(id+"F2.wireOp",EDGE,"E2.1.1.6"),sQuery(id+"F2.wireOp",EDGE,"E2.1.1.7"),sQuery(id+"F2.wireOp",EDGE,"E2.1.1.8"),sQuery(id+"F2.wireOp",EDGE,"E2.1.1.10"),sQuery(id+"F2.wireOp",EDGE,"E2.1.1.11"),sQuery(id+"F2.wireOp",EDGE,"E2.1.1.13"),sQuery(id+"F2.wireOp",EDGE,"E2.1.2.1"),sQuery(id+"F2.wireOp",EDGE,"E2.1.2.2"),sQuery(id+"F2.wireOp",EDGE,"E2.1.2.3"),sQuery(id+"F2.wireOp",EDGE,"E2.1.2.4"),sQuery(id+"F2.wireOp",EDGE,"E2.1.2.5"),sQuery(id+"F2.wireOp",EDGE,"E2.1.2.6"),sQuery(id+"F2.wireOp",EDGE,"E2.1.2.7"),sQuery(id+"F2.wireOp",EDGE,"E2.1.2.8"),sQuery(id+"F2.wireOp",EDGE,"E2.1.2.10"),sQuery(id+"F2.wireOp",EDGE,"E2.1.2.11"),sQuery(id+"F2.wireOp",EDGE,"E2.1.2.13"),sQuery(id+"F2.wireOp",EDGE,"E2.1.3.1"),sQuery(id+"F2.wireOp",EDGE,"E2.1.3.2"),sQuery(id+"F2.wireOp",EDGE,"E2.1.3.3"),sQuery(id+"F2.wireOp",EDGE,"E2.1.3.4"),sQuery(id+"F2.wireOp",EDGE,"E2.1.3.5"),sQuery(id+"F2.wireOp",EDGE,"E2.1.3.10"),sQuery(id+"F2.wireOp",EDGE,"E2.1.3.11"),sQuery(id+"F2.wireOp",EDGE,"E2.1.3.13"),sQuery(id+"F2.wireOp",EDGE,"E2.2.0.7"),sQuery(id+"F2.wireOp",EDGE,"E2.2.0.8"),sQuery(id+"F2.wireOp",EDGE,"E2.2.1.1"),sQuery(id+"F2.wireOp",EDGE,"E2.2.1.2"),sQuery(id+"F2.wireOp",EDGE,"E2.2.1.3"),sQuery(id+"F2.wireOp",EDGE,"E2.2.1.4"),sQuery(id+"F2.wireOp",EDGE,"E2.2.1.5"),sQuery(id+"F2.wireOp",EDGE,"E2.2.1.6"),sQuery(id+"F2.wireOp",EDGE,"E2.2.1.7"),sQuery(id+"F2.wireOp",EDGE,"E2.2.1.8"),sQuery(id+"F2.wireOp",EDGE,"E2.2.1.9"),sQuery(id+"F2.wireOp",EDGE,"E2.2.1.10"),sQuery(id+"F2.wireOp",EDGE,"E2.2.1.11"),sQuery(id+"F2.wireOp",EDGE,"E2.2.1.13"),sQuery(id+"F2.wireOp",EDGE,"E2.2.2.1"),sQuery(id+"F2.wireOp",EDGE,"E2.2.2.2"),sQuery(id+"F2.wireOp",EDGE,"E2.2.2.3"),sQuery(id+"F2.wireOp",EDGE,"E2.2.2.4"),sQuery(id+"F2.wireOp",EDGE,"E2.2.2.5"),sQuery(id+"F2.wireOp",EDGE,"E2.2.2.6"),sQuery(id+"F2.wireOp",EDGE,"E2.2.2.7"),sQuery(id+"F2.wireOp",EDGE,"E2.2.2.8"),sQuery(id+"F2.wireOp",EDGE,"E2.2.2.9"),sQuery(id+"F2.wireOp",EDGE,"E2.2.2.10"),sQuery(id+"F2.wireOp",EDGE,"E2.2.2.11"),sQuery(id+"F2.wireOp",EDGE,"E2.2.2.13"),sQuery(id+"F2.wireOp",EDGE,"E2.2.3.1"),sQuery(id+"F2.wireOp",EDGE,"E2.2.3.2"),sQuery(id+"F2.wireOp",EDGE,"E2.2.3.3"),sQuery(id+"F2.wireOp",EDGE,"E2.2.3.4"),sQuery(id+"F2.wireOp",EDGE,"E2.2.3.5"),sQuery(id+"F2.wireOp",EDGE,"E2.2.3.10"),sQuery(id+"F2.wireOp",EDGE,"E2.2.3.11"),sQuery(id+"F2.wireOp",EDGE,"E2.2.3.13"),sQuery(id+"F2.wireOp",EDGE,"E2.3.0.7"),sQuery(id+"F2.wireOp",EDGE,"E2.3.0.8"),sQuery(id+"F2.wireOp",EDGE,"E2.3.1.1"),sQuery(id+"F2.wireOp",EDGE,"E2.3.1.2"),sQuery(id+"F2.wireOp",EDGE,"E2.3.1.3"),sQuery(id+"F2.wireOp",EDGE,"E2.3.1.4"),sQuery(id+"F2.wireOp",EDGE,"E2.3.1.5"),sQuery(id+"F2.wireOp",EDGE,"E2.3.1.6"),sQuery(id+"F2.wireOp",EDGE,"E2.3.1.7"),sQuery(id+"F2.wireOp",EDGE,"E2.3.1.8"),sQuery(id+"F2.wireOp",EDGE,"E2.3.1.9"),sQuery(id+"F2.wireOp",EDGE,"E2.3.1.10"),sQuery(id+"F2.wireOp",EDGE,"E2.3.1.11"),sQuery(id+"F2.wireOp",EDGE,"E2.3.1.13"),sQuery(id+"F2.wireOp",EDGE,"E2.3.2.1"),sQuery(id+"F2.wireOp",EDGE,"E2.3.2.2"),sQuery(id+"F2.wireOp",EDGE,"E2.3.2.3"),sQuery(id+"F2.wireOp",EDGE,"E2.3.2.4"),sQuery(id+"F2.wireOp",EDGE,"E2.3.2.5"),sQuery(id+"F2.wireOp",EDGE,"E2.3.2.6"),sQuery(id+"F2.wireOp",EDGE,"E2.3.2.7"),sQuery(id+"F2.wireOp",EDGE,"E2.3.2.8"),sQuery(id+"F2.wireOp",EDGE,"E2.3.2.9"),sQuery(id+"F2.wireOp",EDGE,"E2.3.2.10"),sQuery(id+"F2.wireOp",EDGE,"E2.3.2.11"),sQuery(id+"F2.wireOp",EDGE,"E2.3.2.13"),sQuery(id+"F2.wireOp",EDGE,"E2.3.3.1"),sQuery(id+"F2.wireOp",EDGE,"E2.3.3.2"),sQuery(id+"F2.wireOp",EDGE,"E2.3.3.3"),sQuery(id+"F2.wireOp",EDGE,"E2.3.3.4"),sQuery(id+"F2.wireOp",EDGE,"E2.3.3.5"),sQuery(id+"F2.wireOp",EDGE,"E2.3.3.10"),sQuery(id+"F2.wireOp",EDGE,"E2.3.3.11"),sQuery(id+"F2.wireOp",EDGE,"E2.3.3.13"),sQuery(id+"F2.wireOp",EDGE,"E2.4.0.7"),sQuery(id+"F2.wireOp",EDGE,"E2.4.0.8"),sQuery(id+"F2.wireOp",EDGE,"E2.4.1.1"),sQuery(id+"F2.wireOp",EDGE,"E2.4.1.2"),sQuery(id+"F2.wireOp",EDGE,"E2.4.1.3"),sQuery(id+"F2.wireOp",EDGE,"E2.4.1.4"),sQuery(id+"F2.wireOp",EDGE,"E2.4.1.5"),sQuery(id+"F2.wireOp",EDGE,"E2.4.1.6"),sQuery(id+"F2.wireOp",EDGE,"E2.4.1.7"),sQuery(id+"F2.wireOp",EDGE,"E2.4.1.8"),sQuery(id+"F2.wireOp",EDGE,"E2.4.1.9"),sQuery(id+"F2.wireOp",EDGE,"E2.4.1.10"),sQuery(id+"F2.wireOp",EDGE,"E2.4.1.11"),sQuery(id+"F2.wireOp",EDGE,"E2.4.1.13"),sQuery(id+"F2.wireOp",EDGE,"E2.4.2.1"),sQuery(id+"F2.wireOp",EDGE,"E2.4.2.2"),sQuery(id+"F2.wireOp",EDGE,"E2.4.2.3"),sQuery(id+"F2.wireOp",EDGE,"E2.4.2.4"),sQuery(id+"F2.wireOp",EDGE,"E2.4.2.5"),sQuery(id+"F2.wireOp",EDGE,"E2.4.2.6"),sQuery(id+"F2.wireOp",EDGE,"E2.4.2.7"),sQuery(id+"F2.wireOp",EDGE,"E2.4.2.8"),sQuery(id+"F2.wireOp",EDGE,"E2.4.2.9"),sQuery(id+"F2.wireOp",EDGE,"E2.4.2.10"),sQuery(id+"F2.wireOp",EDGE,"E2.4.2.11"),sQuery(id+"F2.wireOp",EDGE,"E2.4.2.13"),sQuery(id+"F2.wireOp",EDGE,"E2.4.3.1"),sQuery(id+"F2.wireOp",EDGE,"E2.4.3.2"),sQuery(id+"F2.wireOp",EDGE,"E2.4.3.3"),sQuery(id+"F2.wireOp",EDGE,"E2.4.3.4"),sQuery(id+"F2.wireOp",EDGE,"E2.4.3.5"),sQuery(id+"F2.wireOp",EDGE,"E2.4.3.10"),sQuery(id+"F2.wireOp",EDGE,"E2.4.3.11"),sQuery(id+"F2.wireOp",EDGE,"E2.4.3.13"),sQuery(id+"F2.wireOp",EDGE,"E2.5.0.7"),sQuery(id+"F2.wireOp",EDGE,"E2.5.0.8"),sQuery(id+"F2.wireOp",EDGE,"E2.5.1.1"),sQuery(id+"F2.wireOp",EDGE,"E2.5.1.2"),sQuery(id+"F2.wireOp",EDGE,"E2.5.1.3"),sQuery(id+"F2.wireOp",EDGE,"E2.5.1.4"),sQuery(id+"F2.wireOp",EDGE,"E2.5.1.5"),sQuery(id+"F2.wireOp",EDGE,"E2.5.1.6"),sQuery(id+"F2.wireOp",EDGE,"E2.5.1.7"),sQuery(id+"F2.wireOp",EDGE,"E2.5.1.8"),sQuery(id+"F2.wireOp",EDGE,"E2.5.1.9"),sQuery(id+"F2.wireOp",EDGE,"E2.5.1.10"),sQuery(id+"F2.wireOp",EDGE,"E2.5.1.11"),sQuery(id+"F2.wireOp",EDGE,"E2.5.1.13"),sQuery(id+"F2.wireOp",EDGE,"E2.5.2.1"),sQuery(id+"F2.wireOp",EDGE,"E2.5.2.2"),sQuery(id+"F2.wireOp",EDGE,"E2.5.2.3"),sQuery(id+"F2.wireOp",EDGE,"E2.5.2.4"),sQuery(id+"F2.wireOp",EDGE,"E2.5.2.5"),sQuery(id+"F2.wireOp",EDGE,"E2.5.2.6"),sQuery(id+"F2.wireOp",EDGE,"E2.5.2.7"),sQuery(id+"F2.wireOp",EDGE,"E2.5.2.8"),sQuery(id+"F2.wireOp",EDGE,"E2.5.2.9"),sQuery(id+"F2.wireOp",EDGE,"E2.5.2.10"),sQuery(id+"F2.wireOp",EDGE,"E2.5.2.11"),sQuery(id+"F2.wireOp",EDGE,"E2.5.2.13"),sQuery(id+"F2.wireOp",EDGE,"E2.5.3.1"),sQuery(id+"F2.wireOp",EDGE,"E2.5.3.2"),sQuery(id+"F2.wireOp",EDGE,"E2.5.3.3"),sQuery(id+"F2.wireOp",EDGE,"E2.5.3.4"),sQuery(id+"F2.wireOp",EDGE,"E2.5.3.5"),sQuery(id+"F2.wireOp",EDGE,"E2.5.3.10"),sQuery(id+"F2.wireOp",EDGE,"E2.5.3.11"),sQuery(id+"F2.wireOp",EDGE,"E2.5.3.13"),sQuery(id+"F2.wireOp",EDGE,"E2.6.0.7"),sQuery(id+"F2.wireOp",EDGE,"E2.6.0.8"),sQuery(id+"F2.wireOp",EDGE,"E2.6.1.2"),sQuery(id+"F2.wireOp",EDGE,"E2.6.1.3"),sQuery(id+"F2.wireOp",EDGE,"E2.6.1.4"),sQuery(id+"F2.wireOp",EDGE,"E2.6.1.7"),sQuery(id+"F2.wireOp",EDGE,"E2.6.1.8"),sQuery(id+"F2.wireOp",EDGE,"E2.6.1.9"),sQuery(id+"F2.wireOp",EDGE,"E2.6.1.10"),sQuery(id+"F2.wireOp",EDGE,"E2.6.1.11"),sQuery(id+"F2.wireOp",EDGE,"E2.6.2.2"),sQuery(id+"F2.wireOp",EDGE,"E2.6.2.3"),sQuery(id+"F2.wireOp",EDGE,"E2.6.2.4"),sQuery(id+"F2.wireOp",EDGE,"E2.6.2.7"),sQuery(id+"F2.wireOp",EDGE,"E2.6.2.8"),sQuery(id+"F2.wireOp",EDGE,"E2.6.2.9"),sQuery(id+"F2.wireOp",EDGE,"E2.6.2.10"),sQuery(id+"F2.wireOp",EDGE,"E2.6.2.11"),sQuery(id+"F2.wireOp",EDGE,"E2.6.3.2"),sQuery(id+"F2.wireOp",EDGE,"E2.6.3.3"),sQuery(id+"F2.wireOp",EDGE,"E2.6.3.4"),sQuery(id+"F2.wireOp",EDGE,"E2.6.3.10"),sQuery(id+"F2.wireOp",EDGE,"E2.6.3.11"),sQuery(id+"F2.wireOp",EDGE,"E3.0"),sQuery(id+"F2.wireOp",EDGE,"E3.1"),sQuery(id+"F2.wireOp",EDGE,"E3.2"),sQuery(id+"F2.wireOp",EDGE,"E3.3"),sQuery(id+"F2.wireOp",EDGE,"E4.trimOffspring"),sQuery(id+"F2.wireOp",EDGE,"E5.trimOffspring"),sQuery(id+"F2.wireOp",EDGE,"E6.trimOffspring"),sQuery(id+"F2.wireOp",EDGE,"E7.trimOffspring"),sQuery(id+"F2.wireOp",EDGE,"E8.trimOffspring"),sQuery(id+"F2.wireOp",EDGE,"E9.trimOffspring"),sQuery(id+"F2.wireOp",EDGE,"E10.trimOffspring"),sQuery(id+"F2.wireOp",EDGE,"E11.trimOffspring"),sQuery(id+"F2.wireOp",EDGE,"E12.trimOffspring"),sQuery(id+"F2.wireOp",EDGE,"E13.trimOffspring"),sQuery(id+"F2.wireOp",EDGE,"E14.trimOffspring"),sQuery(id+"F2.wireOp",EDGE,"E15.trimOffspring"),sQuery(id+"F2.wireOp",EDGE,"E16.trimOffspring"),sQuery(id+"F2.wireOp",EDGE,"E17.trimOffspring"),sQuery(id+"F2.wireOp",EDGE,"E18.trimOffspring"),sQuery(id+"F2.wireOp",EDGE,"E19.trimOffspring"),sQuery(id+"F2.wireOp",EDGE,"E20.trimOffspring"),sQuery(id+"F2.wireOp",EDGE,"E21.trimOffspring"),sQuery(id+"F2.wireOp",EDGE,"E22.trimOffspring"),sQuery(id+"F2.wireOp",EDGE,"E23.trimOffspring"),sQuery(id+"F2.wireOp",EDGE,"E24.trimOffspring"),sQuery(id+"F2.wireOp",EDGE,"E25.trimOffspring"),sQuery(id+"F2.wireOp",EDGE,"E26.0"),sQuery(id+"F2.wireOp",EDGE,"E26.1"),sQuery(id+"F2.wireOp",EDGE,"E26.2"),sQuery(id+"F2.wireOp",EDGE,"E26.3")])],"isStart":false})]});
            extrude(context, id + "F5", {"entities" : qUnion([Q0]), "operationType" : NewBodyOperationType.ADD, "endBound" : BoundingType.UP_TO_SURFACE, "endBoundEntityFace" : qUnion([Q1]), "depth" : 4 * mm});
        }
        {
            var Q0;
            Q0=qCreatedBy(makeId("Top.planeOp"),FACE);
            var sketch = newSketch(context, id + "F6", { "sketchPlane" : qUnion([Q0])});
            skCircle(sketch, "E33.cCircle", {"center": v(72, 0) * mm, "radius": 11.55 * mm, "construction": true});
            skLineSegment(sketch, "E33.1", {"start": v(72, -11.55) * mm, "end": v(62, -5.77) * mm});
            skLineSegment(sketch, "E33.2", {"start": v(62, -5.77) * mm, "end": v(62, 5.77) * mm});
            skLineSegment(sketch, "E33.3", {"start": v(62, 5.77) * mm, "end": v(72, 11.55) * mm});
            skLineSegment(sketch, "E34.0", {"start": v(70, -35.22) * mm, "end": v(70, 35.22) * mm});
            skSolve(sketch);
        }
        {
            var Q0;
            Q0 = qSketchRegion(id + "F6", true);
            var Q1;
            {var subQ0=sQuery(id+"F4.wireOp",EDGE,"E29.0");Q1=makeQuery(id+"F5.boolean.opBoolean","MERGE",FACE,{"derivedFrom":[makeQuery(id+"F3.boolean.opBoolean","MERGE",FACE,{"derivedFrom":[makeQuery(id+"F1.opExtrude","CAP_FACE",FACE,{"disambiguationData":[OSD([sQuery(id+"F0.wireOp",EDGE,"E0.bottom"),sQuery(id+"F0.wireOp",EDGE,"E0.top"),sQuery(id+"F0.wireOp",EDGE,"E0.left"),sQuery(id+"F0.wireOp",EDGE,"E0.right"),sQuery(id+"F0.wireOp",EDGE,"E1.0"),sQuery(id+"F0.wireOp",EDGE,"E1.1"),sQuery(id+"F0.wireOp",EDGE,"E1.2"),sQuery(id+"F0.wireOp",EDGE,"E1.3")])],"isStart":false}),makeQuery(id+"F3.opExtrude","CAP_FACE",FACE,{"disambiguationData":[OSD([sQuery(id+"F2.wireOp",EDGE,"E2.0.1.1"),sQuery(id+"F2.wireOp",EDGE,"E2.0.1.5"),sQuery(id+"F2.wireOp",EDGE,"E2.0.1.13"),sQuery(id+"F2.wireOp",EDGE,"E2.0.2.1"),sQuery(id+"F2.wireOp",EDGE,"E2.0.2.5"),sQuery(id+"F2.wireOp",EDGE,"E2.0.2.13"),sQuery(id+"F2.wireOp",EDGE,"E2.0.3.1"),sQuery(id+"F2.wireOp",EDGE,"E2.0.3.5"),sQuery(id+"F2.wireOp",EDGE,"E2.0.3.13"),sQuery(id+"F2.wireOp",EDGE,"E2.1.0.7"),sQuery(id+"F2.wireOp",EDGE,"E2.1.0.8"),sQuery(id+"F2.wireOp",EDGE,"E2.1.1.1"),sQuery(id+"F2.wireOp",EDGE,"E2.1.1.2"),sQuery(id+"F2.wireOp",EDGE,"E2.1.1.3"),sQuery(id+"F2.wireOp",EDGE,"E2.1.1.4"),sQuery(id+"F2.wireOp",EDGE,"E2.1.1.5"),sQuery(id+"F2.wireOp",EDGE,"E2.1.1.6"),sQuery(id+"F2.wireOp",EDGE,"E2.1.1.7"),sQuery(id+"F2.wireOp",EDGE,"E2.1.1.8"),sQuery(id+"F2.wireOp",EDGE,"E2.1.1.10"),sQuery(id+"F2.wireOp",EDGE,"E2.1.1.11"),sQuery(id+"F2.wireOp",EDGE,"E2.1.1.13"),sQuery(id+"F2.wireOp",EDGE,"E2.1.2.1"),sQuery(id+"F2.wireOp",EDGE,"E2.1.2.2"),sQuery(id+"F2.wireOp",EDGE,"E2.1.2.3"),sQuery(id+"F2.wireOp",EDGE,"E2.1.2.4"),sQuery(id+"F2.wireOp",EDGE,"E2.1.2.5"),sQuery(id+"F2.wireOp",EDGE,"E2.1.2.6"),sQuery(id+"F2.wireOp",EDGE,"E2.1.2.7"),sQuery(id+"F2.wireOp",EDGE,"E2.1.2.8"),sQuery(id+"F2.wireOp",EDGE,"E2.1.2.10"),sQuery(id+"F2.wireOp",EDGE,"E2.1.2.11"),sQuery(id+"F2.wireOp",EDGE,"E2.1.2.13"),sQuery(id+"F2.wireOp",EDGE,"E2.1.3.1"),sQuery(id+"F2.wireOp",EDGE,"E2.1.3.2"),sQuery(id+"F2.wireOp",EDGE,"E2.1.3.3"),sQuery(id+"F2.wireOp",EDGE,"E2.1.3.4"),sQuery(id+"F2.wireOp",EDGE,"E2.1.3.5"),sQuery(id+"F2.wireOp",EDGE,"E2.1.3.10"),sQuery(id+"F2.wireOp",EDGE,"E2.1.3.11"),sQuery(id+"F2.wireOp",EDGE,"E2.1.3.13"),sQuery(id+"F2.wireOp",EDGE,"E2.2.0.7"),sQuery(id+"F2.wireOp",EDGE,"E2.2.0.8"),sQuery(id+"F2.wireOp",EDGE,"E2.2.1.1"),sQuery(id+"F2.wireOp",EDGE,"E2.2.1.2"),sQuery(id+"F2.wireOp",EDGE,"E2.2.1.3"),sQuery(id+"F2.wireOp",EDGE,"E2.2.1.4"),sQuery(id+"F2.wireOp",EDGE,"E2.2.1.5"),sQuery(id+"F2.wireOp",EDGE,"E2.2.1.6"),sQuery(id+"F2.wireOp",EDGE,"E2.2.1.7"),sQuery(id+"F2.wireOp",EDGE,"E2.2.1.8"),sQuery(id+"F2.wireOp",EDGE,"E2.2.1.9"),sQuery(id+"F2.wireOp",EDGE,"E2.2.1.10"),sQuery(id+"F2.wireOp",EDGE,"E2.2.1.11"),sQuery(id+"F2.wireOp",EDGE,"E2.2.1.13"),sQuery(id+"F2.wireOp",EDGE,"E2.2.2.1"),sQuery(id+"F2.wireOp",EDGE,"E2.2.2.2"),sQuery(id+"F2.wireOp",EDGE,"E2.2.2.3"),sQuery(id+"F2.wireOp",EDGE,"E2.2.2.4"),sQuery(id+"F2.wireOp",EDGE,"E2.2.2.5"),sQuery(id+"F2.wireOp",EDGE,"E2.2.2.6"),sQuery(id+"F2.wireOp",EDGE,"E2.2.2.7"),sQuery(id+"F2.wireOp",EDGE,"E2.2.2.8"),sQuery(id+"F2.wireOp",EDGE,"E2.2.2.9"),sQuery(id+"F2.wireOp",EDGE,"E2.2.2.10"),sQuery(id+"F2.wireOp",EDGE,"E2.2.2.11"),sQuery(id+"F2.wireOp",EDGE,"E2.2.2.13"),sQuery(id+"F2.wireOp",EDGE,"E2.2.3.1"),sQuery(id+"F2.wireOp",EDGE,"E2.2.3.2"),sQuery(id+"F2.wireOp",EDGE,"E2.2.3.3"),sQuery(id+"F2.wireOp",EDGE,"E2.2.3.4"),sQuery(id+"F2.wireOp",EDGE,"E2.2.3.5"),sQuery(id+"F2.wireOp",EDGE,"E2.2.3.10"),sQuery(id+"F2.wireOp",EDGE,"E2.2.3.11"),sQuery(id+"F2.wireOp",EDGE,"E2.2.3.13"),sQuery(id+"F2.wireOp",EDGE,"E2.3.0.7"),sQuery(id+"F2.wireOp",EDGE,"E2.3.0.8"),sQuery(id+"F2.wireOp",EDGE,"E2.3.1.1"),sQuery(id+"F2.wireOp",EDGE,"E2.3.1.2"),sQuery(id+"F2.wireOp",EDGE,"E2.3.1.3"),sQuery(id+"F2.wireOp",EDGE,"E2.3.1.4"),sQuery(id+"F2.wireOp",EDGE,"E2.3.1.5"),sQuery(id+"F2.wireOp",EDGE,"E2.3.1.6"),sQuery(id+"F2.wireOp",EDGE,"E2.3.1.7"),sQuery(id+"F2.wireOp",EDGE,"E2.3.1.8"),sQuery(id+"F2.wireOp",EDGE,"E2.3.1.9"),sQuery(id+"F2.wireOp",EDGE,"E2.3.1.10"),sQuery(id+"F2.wireOp",EDGE,"E2.3.1.11"),sQuery(id+"F2.wireOp",EDGE,"E2.3.1.13"),sQuery(id+"F2.wireOp",EDGE,"E2.3.2.1"),sQuery(id+"F2.wireOp",EDGE,"E2.3.2.2"),sQuery(id+"F2.wireOp",EDGE,"E2.3.2.3"),sQuery(id+"F2.wireOp",EDGE,"E2.3.2.4"),sQuery(id+"F2.wireOp",EDGE,"E2.3.2.5"),sQuery(id+"F2.wireOp",EDGE,"E2.3.2.6"),sQuery(id+"F2.wireOp",EDGE,"E2.3.2.7"),sQuery(id+"F2.wireOp",EDGE,"E2.3.2.8"),sQuery(id+"F2.wireOp",EDGE,"E2.3.2.9"),sQuery(id+"F2.wireOp",EDGE,"E2.3.2.10"),sQuery(id+"F2.wireOp",EDGE,"E2.3.2.11"),sQuery(id+"F2.wireOp",EDGE,"E2.3.2.13"),sQuery(id+"F2.wireOp",EDGE,"E2.3.3.1"),sQuery(id+"F2.wireOp",EDGE,"E2.3.3.2"),sQuery(id+"F2.wireOp",EDGE,"E2.3.3.3"),sQuery(id+"F2.wireOp",EDGE,"E2.3.3.4"),sQuery(id+"F2.wireOp",EDGE,"E2.3.3.5"),sQuery(id+"F2.wireOp",EDGE,"E2.3.3.10"),sQuery(id+"F2.wireOp",EDGE,"E2.3.3.11"),sQuery(id+"F2.wireOp",EDGE,"E2.3.3.13"),sQuery(id+"F2.wireOp",EDGE,"E2.4.0.7"),sQuery(id+"F2.wireOp",EDGE,"E2.4.0.8"),sQuery(id+"F2.wireOp",EDGE,"E2.4.1.1"),sQuery(id+"F2.wireOp",EDGE,"E2.4.1.2"),sQuery(id+"F2.wireOp",EDGE,"E2.4.1.3"),sQuery(id+"F2.wireOp",EDGE,"E2.4.1.4"),sQuery(id+"F2.wireOp",EDGE,"E2.4.1.5"),sQuery(id+"F2.wireOp",EDGE,"E2.4.1.6"),sQuery(id+"F2.wireOp",EDGE,"E2.4.1.7"),sQuery(id+"F2.wireOp",EDGE,"E2.4.1.8"),sQuery(id+"F2.wireOp",EDGE,"E2.4.1.9"),sQuery(id+"F2.wireOp",EDGE,"E2.4.1.10"),sQuery(id+"F2.wireOp",EDGE,"E2.4.1.11"),sQuery(id+"F2.wireOp",EDGE,"E2.4.1.13"),sQuery(id+"F2.wireOp",EDGE,"E2.4.2.1"),sQuery(id+"F2.wireOp",EDGE,"E2.4.2.2"),sQuery(id+"F2.wireOp",EDGE,"E2.4.2.3"),sQuery(id+"F2.wireOp",EDGE,"E2.4.2.4"),sQuery(id+"F2.wireOp",EDGE,"E2.4.2.5"),sQuery(id+"F2.wireOp",EDGE,"E2.4.2.6"),sQuery(id+"F2.wireOp",EDGE,"E2.4.2.7"),sQuery(id+"F2.wireOp",EDGE,"E2.4.2.8"),sQuery(id+"F2.wireOp",EDGE,"E2.4.2.9"),sQuery(id+"F2.wireOp",EDGE,"E2.4.2.10"),sQuery(id+"F2.wireOp",EDGE,"E2.4.2.11"),sQuery(id+"F2.wireOp",EDGE,"E2.4.2.13"),sQuery(id+"F2.wireOp",EDGE,"E2.4.3.1"),sQuery(id+"F2.wireOp",EDGE,"E2.4.3.2"),sQuery(id+"F2.wireOp",EDGE,"E2.4.3.3"),sQuery(id+"F2.wireOp",EDGE,"E2.4.3.4"),sQuery(id+"F2.wireOp",EDGE,"E2.4.3.5"),sQuery(id+"F2.wireOp",EDGE,"E2.4.3.10"),sQuery(id+"F2.wireOp",EDGE,"E2.4.3.11"),sQuery(id+"F2.wireOp",EDGE,"E2.4.3.13"),sQuery(id+"F2.wireOp",EDGE,"E2.5.0.7"),sQuery(id+"F2.wireOp",EDGE,"E2.5.0.8"),sQuery(id+"F2.wireOp",EDGE,"E2.5.1.1"),sQuery(id+"F2.wireOp",EDGE,"E2.5.1.2"),sQuery(id+"F2.wireOp",EDGE,"E2.5.1.3"),sQuery(id+"F2.wireOp",EDGE,"E2.5.1.4"),sQuery(id+"F2.wireOp",EDGE,"E2.5.1.5"),sQuery(id+"F2.wireOp",EDGE,"E2.5.1.6"),sQuery(id+"F2.wireOp",EDGE,"E2.5.1.7"),sQuery(id+"F2.wireOp",EDGE,"E2.5.1.8"),sQuery(id+"F2.wireOp",EDGE,"E2.5.1.9"),sQuery(id+"F2.wireOp",EDGE,"E2.5.1.10"),sQuery(id+"F2.wireOp",EDGE,"E2.5.1.11"),sQuery(id+"F2.wireOp",EDGE,"E2.5.1.13"),sQuery(id+"F2.wireOp",EDGE,"E2.5.2.1"),sQuery(id+"F2.wireOp",EDGE,"E2.5.2.2"),sQuery(id+"F2.wireOp",EDGE,"E2.5.2.3"),sQuery(id+"F2.wireOp",EDGE,"E2.5.2.4"),sQuery(id+"F2.wireOp",EDGE,"E2.5.2.5"),sQuery(id+"F2.wireOp",EDGE,"E2.5.2.6"),sQuery(id+"F2.wireOp",EDGE,"E2.5.2.7"),sQuery(id+"F2.wireOp",EDGE,"E2.5.2.8"),sQuery(id+"F2.wireOp",EDGE,"E2.5.2.9"),sQuery(id+"F2.wireOp",EDGE,"E2.5.2.10"),sQuery(id+"F2.wireOp",EDGE,"E2.5.2.11"),sQuery(id+"F2.wireOp",EDGE,"E2.5.2.13"),sQuery(id+"F2.wireOp",EDGE,"E2.5.3.1"),sQuery(id+"F2.wireOp",EDGE,"E2.5.3.2"),sQuery(id+"F2.wireOp",EDGE,"E2.5.3.3"),sQuery(id+"F2.wireOp",EDGE,"E2.5.3.4"),sQuery(id+"F2.wireOp",EDGE,"E2.5.3.5"),sQuery(id+"F2.wireOp",EDGE,"E2.5.3.10"),sQuery(id+"F2.wireOp",EDGE,"E2.5.3.11"),sQuery(id+"F2.wireOp",EDGE,"E2.5.3.13"),sQuery(id+"F2.wireOp",EDGE,"E2.6.0.7"),sQuery(id+"F2.wireOp",EDGE,"E2.6.0.8"),sQuery(id+"F2.wireOp",EDGE,"E2.6.1.2"),sQuery(id+"F2.wireOp",EDGE,"E2.6.1.3"),sQuery(id+"F2.wireOp",EDGE,"E2.6.1.4"),sQuery(id+"F2.wireOp",EDGE,"E2.6.1.7"),sQuery(id+"F2.wireOp",EDGE,"E2.6.1.8"),sQuery(id+"F2.wireOp",EDGE,"E2.6.1.9"),sQuery(id+"F2.wireOp",EDGE,"E2.6.1.10"),sQuery(id+"F2.wireOp",EDGE,"E2.6.1.11"),sQuery(id+"F2.wireOp",EDGE,"E2.6.2.2"),sQuery(id+"F2.wireOp",EDGE,"E2.6.2.3"),sQuery(id+"F2.wireOp",EDGE,"E2.6.2.4"),sQuery(id+"F2.wireOp",EDGE,"E2.6.2.7"),sQuery(id+"F2.wireOp",EDGE,"E2.6.2.8"),sQuery(id+"F2.wireOp",EDGE,"E2.6.2.9"),sQuery(id+"F2.wireOp",EDGE,"E2.6.2.10"),sQuery(id+"F2.wireOp",EDGE,"E2.6.2.11"),sQuery(id+"F2.wireOp",EDGE,"E2.6.3.2"),sQuery(id+"F2.wireOp",EDGE,"E2.6.3.3"),sQuery(id+"F2.wireOp",EDGE,"E2.6.3.4"),sQuery(id+"F2.wireOp",EDGE,"E2.6.3.10"),sQuery(id+"F2.wireOp",EDGE,"E2.6.3.11"),sQuery(id+"F2.wireOp",EDGE,"E3.0"),sQuery(id+"F2.wireOp",EDGE,"E3.1"),sQuery(id+"F2.wireOp",EDGE,"E3.2"),sQuery(id+"F2.wireOp",EDGE,"E3.3"),sQuery(id+"F2.wireOp",EDGE,"E4.trimOffspring"),sQuery(id+"F2.wireOp",EDGE,"E5.trimOffspring"),sQuery(id+"F2.wireOp",EDGE,"E6.trimOffspring"),sQuery(id+"F2.wireOp",EDGE,"E7.trimOffspring"),sQuery(id+"F2.wireOp",EDGE,"E8.trimOffspring"),sQuery(id+"F2.wireOp",EDGE,"E9.trimOffspring"),sQuery(id+"F2.wireOp",EDGE,"E10.trimOffspring"),sQuery(id+"F2.wireOp",EDGE,"E11.trimOffspring"),sQuery(id+"F2.wireOp",EDGE,"E12.trimOffspring"),sQuery(id+"F2.wireOp",EDGE,"E13.trimOffspring"),sQuery(id+"F2.wireOp",EDGE,"E14.trimOffspring"),sQuery(id+"F2.wireOp",EDGE,"E15.trimOffspring"),sQuery(id+"F2.wireOp",EDGE,"E16.trimOffspring"),sQuery(id+"F2.wireOp",EDGE,"E17.trimOffspring"),sQuery(id+"F2.wireOp",EDGE,"E18.trimOffspring"),sQuery(id+"F2.wireOp",EDGE,"E19.trimOffspring"),sQuery(id+"F2.wireOp",EDGE,"E20.trimOffspring"),sQuery(id+"F2.wireOp",EDGE,"E21.trimOffspring"),sQuery(id+"F2.wireOp",EDGE,"E22.trimOffspring"),sQuery(id+"F2.wireOp",EDGE,"E23.trimOffspring"),sQuery(id+"F2.wireOp",EDGE,"E24.trimOffspring"),sQuery(id+"F2.wireOp",EDGE,"E25.trimOffspring"),sQuery(id+"F2.wireOp",EDGE,"E26.0"),sQuery(id+"F2.wireOp",EDGE,"E26.1"),sQuery(id+"F2.wireOp",EDGE,"E26.2"),sQuery(id+"F2.wireOp",EDGE,"E26.3")])],"isStart":false})]}),makeQuery(id+"F5.opExtrude","CAP_FACE",FACE,{"disambiguationData":[OSD([subQ0,sQuery(id+"F4.wireOp",EDGE,"E32.0"),sQuery(id+"F4.wireOp",EDGE,"E32.1"),sQuery(id+"F4.wireOp",EDGE,"E32.2")])],"isStart":false}),makeQuery(id+"F5.opExtrude","CAP_FACE",FACE,{"disambiguationData":[OSD([subQ0,sQuery(id+"F4.wireOp",EDGE,"E31.0"),sQuery(id+"F4.wireOp",EDGE,"E31.1"),sQuery(id+"F4.wireOp",EDGE,"E31.2")])],"isStart":false})]});}
            extrude(context, id + "F7", {"entities" : qUnion([Q0]), "operationType" : NewBodyOperationType.ADD, "endBound" : BoundingType.UP_TO_SURFACE, "endBoundEntityFace" : qUnion([Q1]), "depth" : 25 * mm});
        }
        {
            var Q0;
            Q0=qCreatedBy(makeId("Top.planeOp"),FACE);
            var sketch = newSketch(context, id + "F8", { "sketchPlane" : qUnion([Q0])});
            skCircle(sketch, "E35.cCircle", {"center": v(36, -62.36) * mm, "radius": 11.55 * mm, "construction": true});
            skLineSegment(sketch, "E35.0", {"start": v(36, -73.9) * mm, "end": v(26, -68.13) * mm});
            skLineSegment(sketch, "E35.1", {"start": v(26, -68.13) * mm, "end": v(26, -56.58) * mm});
            skLineSegment(sketch, "E35.2", {"start": v(26, -56.58) * mm, "end": v(36, -50.8) * mm});
            skLineSegment(sketch, "E35.3", {"start": v(36, -50.8) * mm, "end": v(46, -56.58) * mm});
            skLineSegment(sketch, "E35.4", {"start": v(46, -56.58) * mm, "end": v(46, -68.13) * mm});
            skLineSegment(sketch, "E35.5", {"start": v(46, -68.13) * mm, "end": v(36, -73.9) * mm});
            skCircle(sketch, "E36.cCircle", {"center": v(-36, -62.36) * mm, "radius": 11.55 * mm, "construction": true});
            skLineSegment(sketch, "E36.0", {"start": v(-36, -73.9) * mm, "end": v(-46, -68.13) * mm});
            skLineSegment(sketch, "E36.1", {"start": v(-46, -68.13) * mm, "end": v(-46, -56.58) * mm});
            skLineSegment(sketch, "E36.2", {"start": v(-46, -56.58) * mm, "end": v(-36, -50.8) * mm});
            skLineSegment(sketch, "E36.3", {"start": v(-36, -50.8) * mm, "end": v(-26, -56.58) * mm});
            skLineSegment(sketch, "E36.4", {"start": v(-26, -56.58) * mm, "end": v(-26, -68.13) * mm});
            skLineSegment(sketch, "E36.5", {"start": v(-26, -68.13) * mm, "end": v(-36, -73.9) * mm});
            skLineSegment(sketch, "E37.0", {"start": v(62, -5.77) * mm, "end": v(62, 5.77) * mm, "construction": true});
            skLineSegment(sketch, "E37.1", {"start": v(62, 5.77) * mm, "end": v(66, 8.08) * mm, "construction": true});
            skLineSegment(sketch, "E37.2", {"start": v(66, -8.08) * mm, "end": v(62, -5.77) * mm, "construction": true});
            skCircle(sketch, "E38.cCircle", {"center": v(72, 0) * mm, "radius": 11.55 * mm, "construction": true});
            skLineSegment(sketch, "E38.0", {"start": v(72, -11.55) * mm, "end": v(62, -5.77) * mm, "construction": true});
            skLineSegment(sketch, "E38.2", {"start": v(62, 5.77) * mm, "end": v(72, 11.55) * mm, "construction": true});
            skLineSegment(sketch, "E38.3", {"start": v(72, 11.55) * mm, "end": v(82, 5.77) * mm, "construction": true});
            skLineSegment(sketch, "E38.4", {"start": v(82, 5.77) * mm, "end": v(82, -5.77) * mm, "construction": true});
            skLineSegment(sketch, "E38.5", {"start": v(82, -5.77) * mm, "end": v(72, -11.55) * mm, "construction": true});
            skLineSegment(sketch, "E39.0", {"start": v(65, 4.04) * mm, "end": v(73.5, 8.95) * mm});
            skLineSegment(sketch, "E39.1", {"start": v(65, -4.04) * mm, "end": v(65, 4.04) * mm});
            skLineSegment(sketch, "E39.2", {"start": v(73.5, -8.95) * mm, "end": v(65, -4.04) * mm});
            skLineSegment(sketch, "E40.0", {"start": v(70, -35.22) * mm, "end": v(70, 35.22) * mm});
            skSolve(sketch);
        }
        {
            var Q0;
            Q0 = qSketchRegion(id + "F8", true);
            extrude(context, id + "F9", {"entities" : qUnion([Q0]), "operationType" : NewBodyOperationType.REMOVE, "endBound" : BoundingType.THROUGH_ALL, "depth" : 25 * mm});
        }
    });
